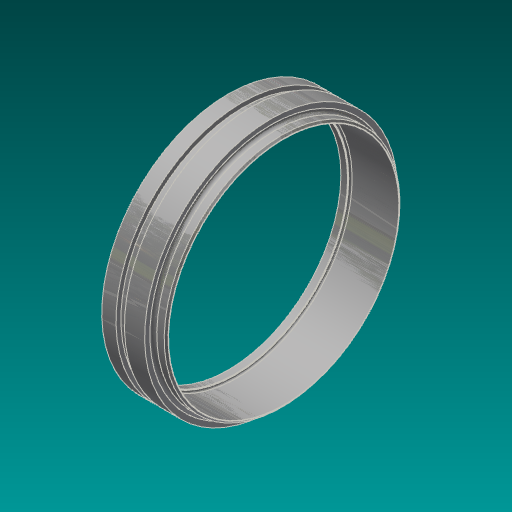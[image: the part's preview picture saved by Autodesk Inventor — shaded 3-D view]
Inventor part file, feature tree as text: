
AUTODESK INVENTOR PART (.ipt)
format: ipt  version: 2017.3 (Build 213257000, 257)  size: 235,520 bytes
history: native  units: in
note: dims shown in document units (in); Inventor stores cm internally (conversion verified against a paired STEP export)
features: revolve x1, chamfer x1, sketch x1
ambient origin geometry x8: Origin, YZ Plane, XZ Plane, XY Plane, X Axis, Y Axis, Z Axis, Center Point
bodies: Solid1 (feature_tree)
feature tree (3):
  revolve  "Revolution1"  [1 undecoded]
  chamfer  "Chamfer2"  Distance=0.3125in
  sketch  "Sketch1"  dims[d0=18.25in d3=17.0in d5=0.3125in d10=0.25in d12=16.25in d13=2.05in d16=90.0deg d17=0.375in d29=0.0312in d30=0.125in d31=45.0deg d35=1.0in d38=0.0687in d39=0.1374in d40=0.895in d41=0.6in d44=8.0in d45=0.2577in d47=0.375in d55=16.625in d58=0.5in d59=6.1875in]
note: 1 required parameter value undecoded (feature->parameter linkage not recoverable at this tier; creation-order binding heuristic only, values carry confidence <= 0.55)
